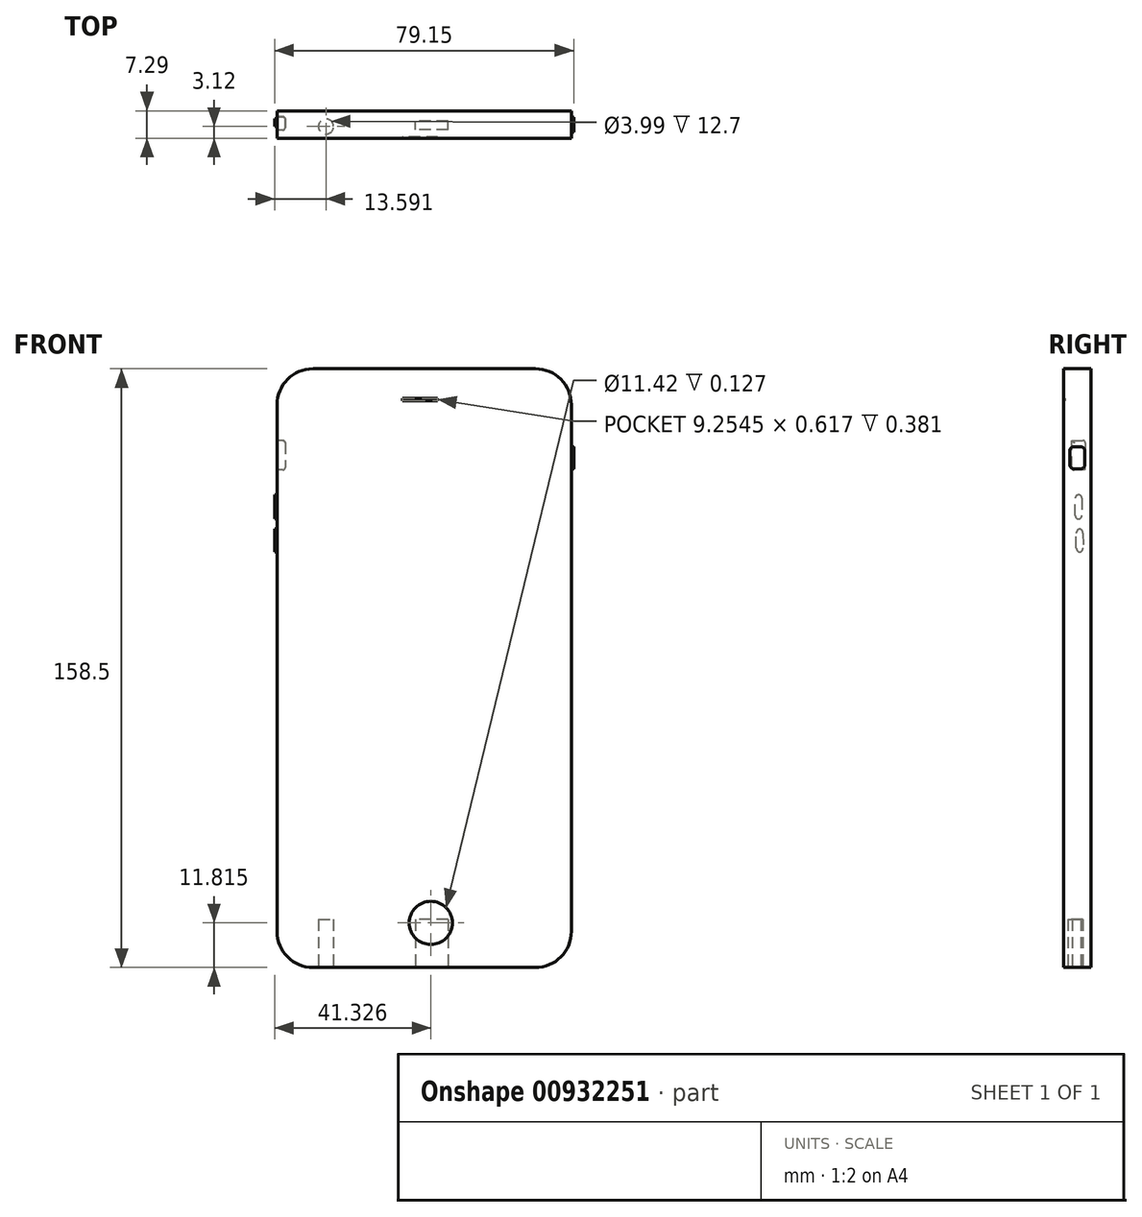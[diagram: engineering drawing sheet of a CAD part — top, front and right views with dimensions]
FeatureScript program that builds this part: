
annotation { "Feature Type Name" : "Feature", "Feature Type Description" : "" }
export const myFeature = defineFeature(function(context is Context, id is Id, definition is map)
    precondition{}
    {
        {
            var Q0;
            Q0=qCreatedBy(makeId("Front.planeOp"),FACE);
            var sketch = newSketch(context, id + "F0", { "sketchPlane" : qUnion([Q0])});
            skLineSegment(sketch, "E0.bottom", {"start": v(-49.87, -74.7) * mm, "end": v(28.01, -74.7) * mm});
            skLineSegment(sketch, "E0.top", {"start": v(-49.87, 83.79) * mm, "end": v(28.01, 83.79) * mm});
            skLineSegment(sketch, "E0.left", {"start": v(-49.87, -74.7) * mm, "end": v(-49.87, 83.79) * mm});
            skLineSegment(sketch, "E0.right", {"start": v(28.01, -74.7) * mm, "end": v(28.01, 83.79) * mm});
            skSolve(sketch);
        }
        {
            var Q0;
            Q0 = qSketchRegion(id + "F0", true);
            extrude(context, id + "F1", {"entities" : qUnion([Q0]), "depth" : 7.3 * mm, "offsetDistance" : 25.4 * mm});
        }
        {
            var Q0;
            Q0=makeQuery(id+"F1.opExtrude","SWEPT_EDGE",EDGE,{"disambiguationData":[OSD([sQuery(id+"F0.wireOp",EDGE,"E0.top"),sQuery(id+"F0.wireOp",EDGE,"E0.left")])]});
            var Q1;
            Q1=makeQuery(id+"F1.opExtrude","SWEPT_EDGE",EDGE,{"disambiguationData":[OSD([sQuery(id+"F0.wireOp",EDGE,"E0.top"),sQuery(id+"F0.wireOp",EDGE,"E0.right")])]});
            var Q2;
            Q2=makeQuery(id+"F1.opExtrude","SWEPT_EDGE",EDGE,{"disambiguationData":[OSD([sQuery(id+"F0.wireOp",EDGE,"E0.bottom"),sQuery(id+"F0.wireOp",EDGE,"E0.right")])]});
            var Q3;
            Q3=makeQuery(id+"F1.opExtrude","SWEPT_EDGE",EDGE,{"disambiguationData":[OSD([sQuery(id+"F0.wireOp",EDGE,"E0.bottom"),sQuery(id+"F0.wireOp",EDGE,"E0.left")])]});
            fillet(context, id + "F2", {"entities" : qUnion([Q0, Q1, Q2, Q3]), "radius" : 9.52 * mm, "tangentPropagation" : true, "allowEdgeOverflow" : false});
        }
        {
            var Q0;
            Q0=makeQuery(id+"F1.opExtrude","CAP_FACE",FACE,{"disambiguationData":[OSD([sQuery(id+"F0.wireOp",EDGE,"E0.bottom"),sQuery(id+"F0.wireOp",EDGE,"E0.top"),sQuery(id+"F0.wireOp",EDGE,"E0.left"),sQuery(id+"F0.wireOp",EDGE,"E0.right")])],"isStart":false});
            var sketch = newSketch(context, id + "F3", { "sketchPlane" : qUnion([Q0])});
            skCircle(sketch, "E1", {"center": v(-9.17, -62.9) * mm, "radius": 5.7 * mm});
            skPoint(sketch, "E1.first.point", {"position": v(-12.9, -67.23) * mm});
            skPoint(sketch, "E1.second.point", {"position": v(-3.73, -64.6) * mm});
            skPoint(sketch, "E1.third.point", {"position": v(-9.4, -57.2) * mm});
            skSolve(sketch);
        }
        {
            var Q0;
            Q0 = qSketchRegion(id + "F3", true);
            extrude(context, id + "F4", {"entities" : qUnion([Q0]), "operationType" : NewBodyOperationType.REMOVE, "oppositeDirection" : true, "depth" : 0.13 * mm, "offsetDistance" : 25.4 * mm});
        }
        {
            var Q0;
            Q0=makeQuery(id+"F1.opExtrude","CAP_FACE",FACE,{"disambiguationData":[OSD([sQuery(id+"F0.wireOp",EDGE,"E0.bottom"),sQuery(id+"F0.wireOp",EDGE,"E0.top"),sQuery(id+"F0.wireOp",EDGE,"E0.left"),sQuery(id+"F0.wireOp",EDGE,"E0.right")])],"isStart":false});
            var sketch = newSketch(context, id + "F5", { "sketchPlane" : qUnion([Q0])});
            skLineSegment(sketch, "E2.bottom", {"start": v(-7.38, 75.95) * mm, "end": v(-16.63, 75.95) * mm});
            skLineSegment(sketch, "E2.top", {"start": v(-7.38, 75.34) * mm, "end": v(-16.63, 75.34) * mm});
            skLineSegment(sketch, "E2.left", {"start": v(-7.38, 75.95) * mm, "end": v(-7.38, 75.34) * mm});
            skLineSegment(sketch, "E2.right", {"start": v(-16.63, 75.95) * mm, "end": v(-16.63, 75.34) * mm});
            skPoint(sketch, "E2.middle", {"position": v(-12, 75.64) * mm});
            skSolve(sketch);
        }
        {
            var Q0;
            Q0 = qSketchRegion(id + "F5", true);
            extrude(context, id + "F6", {"entities" : qUnion([Q0]), "operationType" : NewBodyOperationType.REMOVE, "oppositeDirection" : true, "depth" : 0.38 * mm, "offsetDistance" : 25.4 * mm});
        }
        {
            var Q0;
            Q0=makeQuery(id+"F1.opExtrude","SWEPT_FACE",FACE,{"disambiguationData":[OSD([sQuery(id+"F0.wireOp",EDGE,"E0.right")])]});
            var sketch = newSketch(context, id + "F7", { "sketchPlane" : qUnion([Q0])});
            skLineSegment(sketch, "E3", {"start": v(-5.6, 63.13) * mm, "end": v(-1.67, 63.13) * mm});
            skLineSegment(sketch, "E4", {"start": v(-1.67, 63.13) * mm, "end": v(-1.67, 57.33) * mm});
            skLineSegment(sketch, "E5", {"start": v(-1.67, 57.33) * mm, "end": v(-5.58, 57.33) * mm});
            skLineSegment(sketch, "E6", {"start": v(-5.58, 57.33) * mm, "end": v(-5.6, 63.13) * mm});
            skSolve(sketch);
        }
        {
            var Q0;
            Q0 = qSketchRegion(id + "F7", true);
            extrude(context, id + "F8", {"entities" : qUnion([Q0]), "operationType" : NewBodyOperationType.ADD, "depth" : 0.64 * mm, "offsetDistance" : 25.4 * mm});
        }
        {
            var Q0;
            Q0=makeQuery(id+"F8.opExtrude","SWEPT_EDGE",EDGE,{"disambiguationData":[OSD([sQuery(id+"F7.wireOp",EDGE,"E3"),sQuery(id+"F7.wireOp",EDGE,"E6")])]});
            var Q1;
            Q1=makeQuery(id+"F8.opExtrude","SWEPT_EDGE",EDGE,{"disambiguationData":[OSD([sQuery(id+"F7.wireOp",EDGE,"E5"),sQuery(id+"F7.wireOp",EDGE,"E6")])]});
            var Q2;
            Q2=makeQuery(id+"F8.opExtrude","SWEPT_EDGE",EDGE,{"disambiguationData":[OSD([sQuery(id+"F7.wireOp",EDGE,"E3"),sQuery(id+"F7.wireOp",EDGE,"E4")])]});
            var Q3;
            Q3=makeQuery(id+"F8.opExtrude","SWEPT_EDGE",EDGE,{"disambiguationData":[OSD([sQuery(id+"F7.wireOp",EDGE,"E4"),sQuery(id+"F7.wireOp",EDGE,"E5")])]});
            fillet(context, id + "F9", {"entities" : qUnion([Q0, Q1, Q2, Q3]), "radius" : 1.02 * mm, "tangentPropagation" : true, "allowEdgeOverflow" : false});
        }
        {
            var Q0;
            Q0=makeQuery(id+"F1.opExtrude","SWEPT_FACE",FACE,{"disambiguationData":[OSD([sQuery(id+"F0.wireOp",EDGE,"E0.bottom")])]});
            var sketch = newSketch(context, id + "F10", { "sketchPlane" : qUnion([Q0])});
            skCircle(sketch, "E7", {"center": v(-36.9, 4.17) * mm, "radius": 2 * mm});
            skPoint(sketch, "E7.first.point", {"position": v(-34.92, 4.05) * mm});
            skPoint(sketch, "E7.second.point", {"position": v(-38.9, 4.06) * mm});
            skPoint(sketch, "E7.third.point", {"position": v(-38.33, 5.57) * mm});
            skSolve(sketch);
        }
        {
            var Q0;
            Q0 = qSketchRegion(id + "F10", true);
            extrude(context, id + "F11", {"entities" : qUnion([Q0]), "operationType" : NewBodyOperationType.REMOVE, "oppositeDirection" : true, "depth" : 12.7 * mm, "offsetDistance" : 25.4 * mm});
        }
        {
            var Q0;
            Q0=makeQuery(id+"F1.opExtrude","SWEPT_FACE",FACE,{"disambiguationData":[OSD([sQuery(id+"F0.wireOp",EDGE,"E0.bottom")])]});
            var sketch = newSketch(context, id + "F12", { "sketchPlane" : qUnion([Q0])});
            skCircle(sketch, "E8", {"center": v(-32.6, 3.21) * mm, "radius": 1.3 * mm});
            skPoint(sketch, "E8.first.point", {"position": v(-33.5, 4.15) * mm});
            skPoint(sketch, "E8.second.point", {"position": v(-31.36, 2.81) * mm});
            skPoint(sketch, "E8.third.point", {"position": v(-31.3, 3.37) * mm});
            skSolve(sketch);
        }
        {
            var Q0;
            Q0=makeQuery(id+"F12.imprint","IMPRINT",FACE,{"disambiguationData":[TD([[makeQuery(id+"F12.imprint","IMPRINT",EDGE,{"derivedFrom":sQuery(id+"F12.wireOp",EDGE,"E8")}),-1.0]])]});
            var sketch = newSketch(context, id + "F13", { "sketchPlane" : qUnion([Q0])});
            skLineSegment(sketch, "E9.bottom", {"start": v(-4.6, 5) * mm, "end": v(-13.24, 5) * mm});
            skLineSegment(sketch, "E9.top", {"start": v(-4.6, 2.74) * mm, "end": v(-13.24, 2.74) * mm});
            skLineSegment(sketch, "E9.left", {"start": v(-4.6, 5) * mm, "end": v(-4.6, 2.74) * mm});
            skLineSegment(sketch, "E9.right", {"start": v(-13.24, 5) * mm, "end": v(-13.24, 2.74) * mm});
            skPoint(sketch, "E9.middle", {"position": v(-8.92, 3.87) * mm});
            skSolve(sketch);
        }
        {
            var Q0;
            Q0 = qSketchRegion(id + "F13", true);
            extrude(context, id + "F14", {"entities" : qUnion([Q0]), "operationType" : NewBodyOperationType.REMOVE, "oppositeDirection" : true, "depth" : 12.7 * mm, "offsetDistance" : 25.4 * mm});
        }
        {
            var Q0;
            Q0=makeQuery(id+"F1.opExtrude","SWEPT_FACE",FACE,{"disambiguationData":[OSD([sQuery(id+"F0.wireOp",EDGE,"E0.left")])]});
            var sketch = newSketch(context, id + "F15", { "sketchPlane" : qUnion([Q0])});
            skLineSegment(sketch, "E10", {"start": v(1.61, 56.98) * mm, "end": v(5.1, 56.98) * mm});
            skLineSegment(sketch, "E11", {"start": v(5.1, 56.98) * mm, "end": v(5.1, 64.81) * mm});
            skLineSegment(sketch, "E12", {"start": v(5.1, 64.81) * mm, "end": v(1.52, 64.81) * mm});
            skLineSegment(sketch, "E13", {"start": v(1.52, 64.81) * mm, "end": v(1.61, 56.98) * mm});
            skSolve(sketch);
        }
        {
            var Q0;
            Q0 = qSketchRegion(id + "F15", true);
            extrude(context, id + "F16", {"entities" : qUnion([Q0]), "operationType" : NewBodyOperationType.REMOVE, "oppositeDirection" : true, "depth" : 2.16 * mm, "offsetDistance" : 25.4 * mm});
        }
        {
            var Q0;
            Q0=makeQuery(id+"F1.opExtrude","SWEPT_FACE",FACE,{"disambiguationData":[OSD([sQuery(id+"F0.wireOp",EDGE,"E0.left")])]});
            var sketch = newSketch(context, id + "F17", { "sketchPlane" : qUnion([Q0])});
            skLineSegment(sketch, "E14", {"start": v(2.45, 44.05) * mm, "end": v(4.17, 44.05) * mm});
            skLineSegment(sketch, "E15", {"start": v(4.17, 44.05) * mm, "end": v(4.17, 50.4) * mm});
            skLineSegment(sketch, "E16", {"start": v(4.17, 50.4) * mm, "end": v(2.37, 50.4) * mm});
            skLineSegment(sketch, "E17", {"start": v(2.37, 50.4) * mm, "end": v(2.45, 44.05) * mm});
            skSolve(sketch);
        }
        {
            var Q0;
            Q0 = qSketchRegion(id + "F17", true);
            extrude(context, id + "F18", {"entities" : qUnion([Q0]), "operationType" : NewBodyOperationType.ADD, "depth" : 0.64 * mm, "offsetDistance" : 25.4 * mm});
        }
        {
            var Q0;
            Q0=makeQuery(id+"F18.opExtrude","SWEPT_EDGE",EDGE,{"disambiguationData":[OSD([sQuery(id+"F17.wireOp",EDGE,"E16"),sQuery(id+"F17.wireOp",EDGE,"E17")])]});
            var Q1;
            Q1=makeQuery(id+"F18.opExtrude","SWEPT_EDGE",EDGE,{"disambiguationData":[OSD([sQuery(id+"F17.wireOp",EDGE,"E15"),sQuery(id+"F17.wireOp",EDGE,"E16")])]});
            var Q2;
            Q2=makeQuery(id+"F18.opExtrude","SWEPT_EDGE",EDGE,{"disambiguationData":[OSD([sQuery(id+"F17.wireOp",EDGE,"E14"),sQuery(id+"F17.wireOp",EDGE,"E17")])]});
            var Q3;
            Q3=makeQuery(id+"F18.opExtrude","SWEPT_EDGE",EDGE,{"disambiguationData":[OSD([sQuery(id+"F17.wireOp",EDGE,"E14"),sQuery(id+"F17.wireOp",EDGE,"E15")])]});
            fillet(context, id + "F19", {"entities" : qUnion([Q0, Q1, Q2, Q3]), "radius" : 0.89 * mm, "tangentPropagation" : true, "allowEdgeOverflow" : false});
        }
        {
            var Q0;
            Q0=makeQuery(id+"F1.opExtrude","SWEPT_FACE",FACE,{"disambiguationData":[OSD([sQuery(id+"F0.wireOp",EDGE,"E0.left")])]});
            var sketch = newSketch(context, id + "F20", { "sketchPlane" : qUnion([Q0])});
            skLineSegment(sketch, "E18", {"start": v(2.09, 35.24) * mm, "end": v(3.89, 35.24) * mm});
            skLineSegment(sketch, "E19", {"start": v(3.89, 35.24) * mm, "end": v(3.89, 41.42) * mm});
            skLineSegment(sketch, "E20", {"start": v(3.89, 41.42) * mm, "end": v(2.1, 41.42) * mm});
            skLineSegment(sketch, "E21", {"start": v(2.1, 41.42) * mm, "end": v(2.09, 35.24) * mm});
            skSolve(sketch);
        }
        {
            var Q0;
            Q0 = qSketchRegion(id + "F20", true);
            extrude(context, id + "F21", {"entities" : qUnion([Q0]), "operationType" : NewBodyOperationType.ADD, "depth" : 0.64 * mm, "offsetDistance" : 25.4 * mm});
        }
        {
            var Q0;
            Q0=makeQuery(id+"F21.opExtrude","SWEPT_EDGE",EDGE,{"disambiguationData":[OSD([sQuery(id+"F20.wireOp",EDGE,"E20"),sQuery(id+"F20.wireOp",EDGE,"E21")])]});
            var Q1;
            Q1=makeQuery(id+"F21.opExtrude","SWEPT_EDGE",EDGE,{"disambiguationData":[OSD([sQuery(id+"F20.wireOp",EDGE,"E19"),sQuery(id+"F20.wireOp",EDGE,"E20")])]});
            var Q2;
            Q2=makeQuery(id+"F21.opExtrude","SWEPT_EDGE",EDGE,{"disambiguationData":[OSD([sQuery(id+"F20.wireOp",EDGE,"E18"),sQuery(id+"F20.wireOp",EDGE,"E21")])]});
            var Q3;
            Q3=makeQuery(id+"F21.opExtrude","SWEPT_EDGE",EDGE,{"disambiguationData":[OSD([sQuery(id+"F20.wireOp",EDGE,"E18"),sQuery(id+"F20.wireOp",EDGE,"E19")])]});
            fillet(context, id + "F22", {"entities" : qUnion([Q0, Q1, Q2, Q3]), "radius" : 1.14 * mm, "tangentPropagation" : true, "allowEdgeOverflow" : false});
        }
        {
            var Q0;
            Q0=makeQuery(id+"F16.boolean.opBoolean","COPY",FACE,{"derivedFrom":makeQuery(id+"F16.opExtrude","CAP_FACE",FACE,{"disambiguationData":[OSD([sQuery(id+"F15.wireOp",EDGE,"E10"),sQuery(id+"F15.wireOp",EDGE,"E11"),sQuery(id+"F15.wireOp",EDGE,"E12"),sQuery(id+"F15.wireOp",EDGE,"E13")])],"isStart":false})});
            var Q1;
            Q1=makeQuery(id+"F16.boolean.opBoolean","COPY",EDGE,{"derivedFrom":makeQuery(id+"F16.opExtrude","CAP_EDGE",EDGE,{"disambiguationData":[OSD([sQuery(id+"F15.wireOp",EDGE,"E13")])],"isStart":true})});
            var Q2;
            Q2=makeQuery(id+"F16.boolean.opBoolean","COPY",EDGE,{"derivedFrom":makeQuery(id+"F16.opExtrude","SWEPT_EDGE",EDGE,{"disambiguationData":[OSD([sQuery(id+"F15.wireOp",EDGE,"E10"),sQuery(id+"F15.wireOp",EDGE,"E11")])]})});
            var Q3;
            Q3=makeQuery(id+"F16.boolean.opBoolean","COPY",EDGE,{"derivedFrom":makeQuery(id+"F16.opExtrude","SWEPT_EDGE",EDGE,{"disambiguationData":[OSD([sQuery(id+"F15.wireOp",EDGE,"E12"),sQuery(id+"F15.wireOp",EDGE,"E13")])]})});
            var Q4;
            Q4=makeQuery(id+"F16.boolean.opBoolean","COPY",EDGE,{"derivedFrom":makeQuery(id+"F16.opExtrude","CAP_EDGE",EDGE,{"disambiguationData":[OSD([sQuery(id+"F15.wireOp",EDGE,"E11")])],"isStart":true})});
            fillet(context, id + "F23", {"entities" : qUnion([Q0, Q1, Q2, Q3, Q4]), "radius" : 0.64 * mm, "tangentPropagation" : true, "allowEdgeOverflow" : false});
        }
    });
